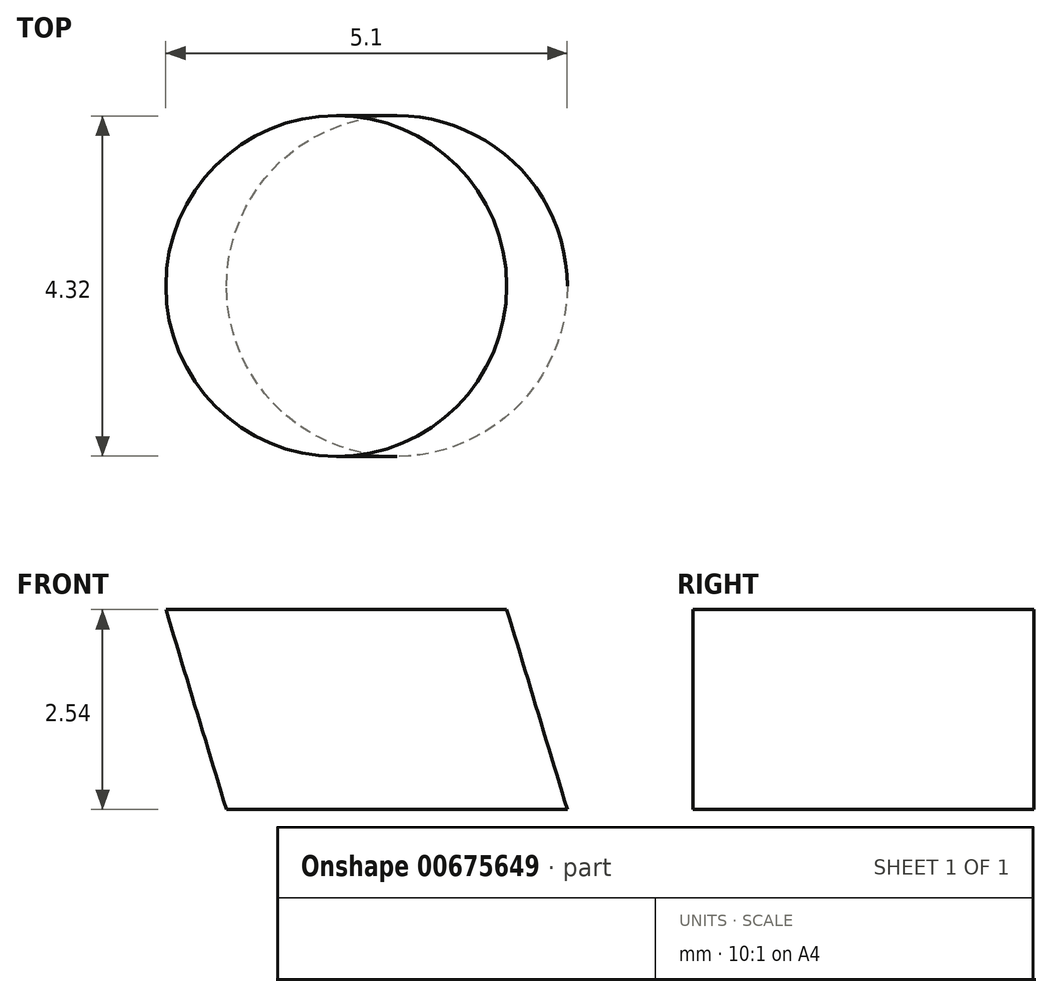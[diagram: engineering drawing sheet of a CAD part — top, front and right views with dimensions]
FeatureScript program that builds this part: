
annotation { "Feature Type Name" : "Feature", "Feature Type Description" : "" }
export const myFeature = defineFeature(function(context is Context, id is Id, definition is map)
    precondition{}
    {
        {
            var Q0;
            Q0=qCreatedBy(makeId("Front.planeOp"),FACE);
            var sketch = newSketch(context, id + "F0", { "sketchPlane" : qUnion([Q0])});
            skFitSpline(sketch, "E0", {"points": [v(-76.25, 0) * mm, v(-47.07, -49.78) * mm, v(0, 54.6) * mm, v(36.25, -50.98) * mm, v(75.95, 0) * mm, v(64.22, -4.66) * mm], "startDerivative": vector(144.55, -477.46) * mm, "endDerivative": vector(-192.02, -140.87) * mm});
            skSolve(sketch);
        }
        {
            var Q0;
            Q0=qCreatedBy(makeId("Top.planeOp"),FACE);
            var sketch = newSketch(context, id + "F1", { "sketchPlane" : qUnion([Q0])});
            skCircle(sketch, "E1", {"center": v(-76.26, 0) * mm, "radius": 2.16 * mm});
            skSolve(sketch);
        }
        {
            var Q0;
            Q0=makeQuery(id+"F1.imprint","IMPRINT",FACE,{"disambiguationData":[TD([[makeQuery(id+"F1.imprint","IMPRINT",EDGE,{"derivedFrom":sQuery(id+"F1.wireOp",EDGE,"E1")}),1.0]])]});
            var Q1;
            Q1=sQuery(id+"F0.wireOp",EDGE,"E0");
            sweep(context, id + "F2", {"profiles" : qUnion([Q0]), "path" : qUnion([Q1])});
        }
        {
            var Q0;
            Q0=makeQuery(id+"F2.opSweep","SWEPT_FACE",FACE,{"disambiguationData":[OSD([sQuery(id+"F0.wireOp",EDGE,"E0"),sQuery(id+"F1.wireOp",EDGE,"E1")])]});
            var Q1;
            Q1=makeQuery(id+"F2.opSweep","CAP_FACE",FACE,{"disambiguationData":[OSD([sQuery(id+"F0.wireOp",VERTEX,"E0.end"),sQuery(id+"F1.wireOp",EDGE,"E1")])],"isStart":false});
            shell(context, id + "F3", {"entities" : qUnion([Q0, Q1]), "thickness" : 2.54 * mm});
        }
    });
